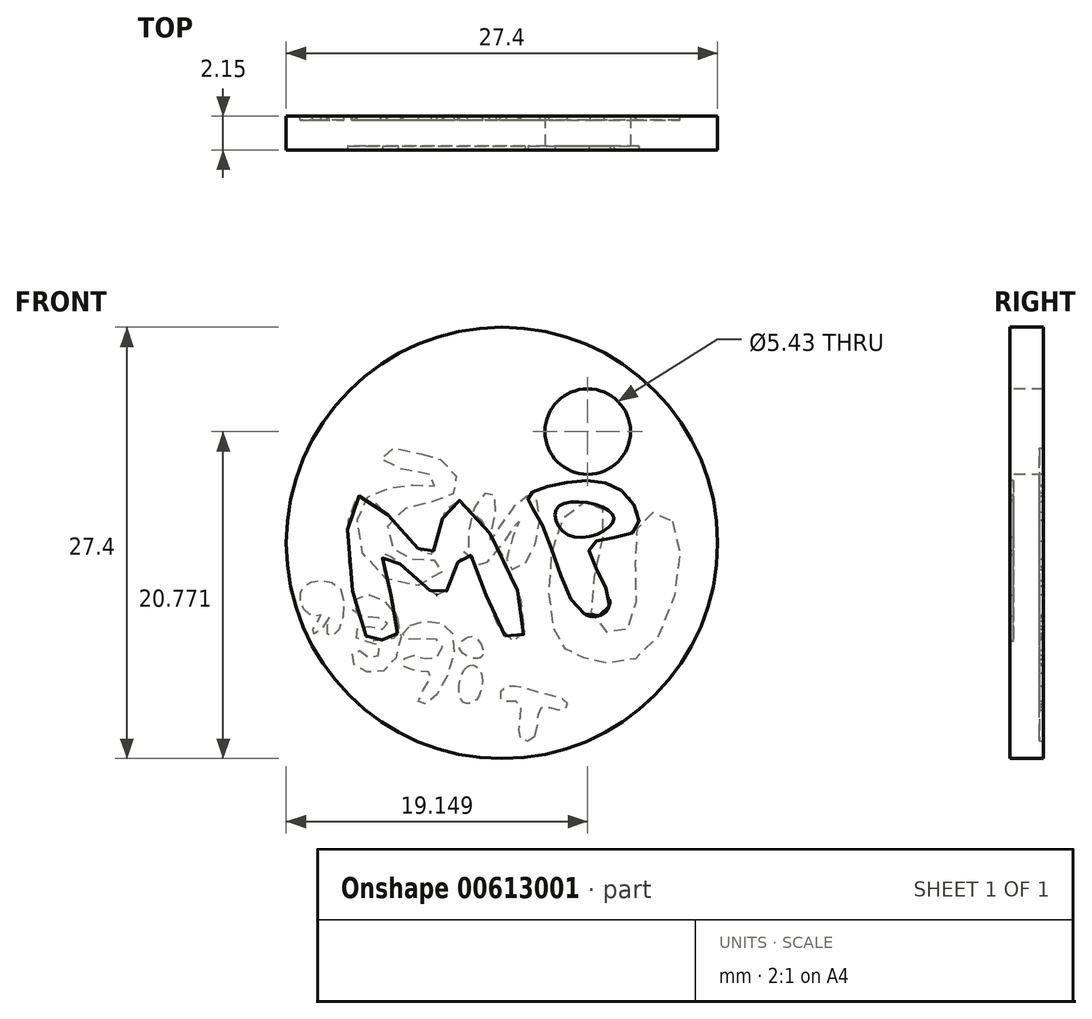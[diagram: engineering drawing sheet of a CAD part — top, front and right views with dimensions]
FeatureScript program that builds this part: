
annotation { "Feature Type Name" : "Feature", "Feature Type Description" : "" }
export const myFeature = defineFeature(function(context is Context, id is Id, definition is map)
    precondition{}
    {
        {
            var Q0;
            Q0=qCreatedBy(makeId("Front.planeOp"),FACE);
            var sketch = newSketch(context, id + "F0", { "sketchPlane" : qUnion([Q0])});
            skCircle(sketch, "E0", {"center": v(15.74, 15.61) * mm, "radius": 13.7 * mm});
            skPoint(sketch, "E1", {"position": v(16, 29.31) * mm});
            skPoint(sketch, "E2", {"position": v(16, 1.91) * mm});
            skSolve(sketch);
        }
        {
            var Q0;
            Q0 = qSketchRegion(id + "F0", true);
            extrude(context, id + "F1", {"entities" : qUnion([Q0]), "depth" : 2.15 * mm, "offsetDistance" : 25 * mm});
        }
        {
            var Q0;
            Q0=makeQuery(id+"F1.opExtrude","CAP_FACE",FACE,{"disambiguationData":[OSD([sQuery(id+"F0.wireOp",EDGE,"E0")])],"isStart":false});
            var sketch = newSketch(context, id + "F2", { "sketchPlane" : qUnion([Q0])});
            skCircle(sketch, "E3", {"center": v(21.19, 22.68) * mm, "radius": 2.71 * mm});
            skSolve(sketch);
        }
        {
            var Q0;
            Q0=makeQuery(id+"F2.imprint","IMPRINT",FACE,{"disambiguationData":[TD([[makeQuery(id+"F2.imprint","IMPRINT",EDGE,{"derivedFrom":sQuery(id+"F2.wireOp",EDGE,"E3")}),1.0]])]});
            extrude(context, id + "F3", {"entities" : qUnion([Q0]), "operationType" : NewBodyOperationType.REMOVE, "endBound" : BoundingType.UP_TO_NEXT, "oppositeDirection" : true, "depth" : 25 * mm, "offsetDistance" : 25 * mm});
        }
        {
            var Q0;
            Q0=makeQuery(id+"F1.opExtrude","CAP_FACE",FACE,{"disambiguationData":[OSD([sQuery(id+"F0.wireOp",EDGE,"E0")])],"isStart":false});
            var sketch = newSketch(context, id + "F4", { "sketchPlane" : qUnion([Q0])});
            skFitSpline(sketch, "E4", {"points": [v(7.1, 9.7) * mm, v(6.53, 18.53) * mm, v(10.66, 15.05) * mm, v(11.38, 15.08) * mm, v(12.81, 18.35) * mm, v(17.2, 10.16) * mm, v(16.05, 9.59) * mm, v(13.5, 15.08) * mm, v(12.27, 12.64) * mm, v(11.41, 12.42) * mm, v(8.21, 14.83) * mm, v(9.11, 9.87) * mm, v(8.1, 9.44) * mm, v(7.1, 9.7) * mm]});
            skFitSpline(sketch, "E5", {"points": [v(20.97, 11.1) * mm, v(18.24, 16.92) * mm, v(17.41, 18.57) * mm, v(19.93, 19.47) * mm, v(23.49, 18.82) * mm, v(24.2, 16.38) * mm, v(21.33, 15.44) * mm, v(22.59, 11.78) * mm, v(20.97, 11.1) * mm]});
            skFitSpline(sketch, "E6", {"points": [v(19.35, 17.96) * mm, v(20.18, 16.02) * mm, v(22.84, 17.27) * mm, v(19.35, 17.96) * mm]});
            skSolve(sketch);
        }
        {
            var Q0;
            Q0=makeQuery(id+"F4.imprint","IMPRINT",FACE,{"disambiguationData":[TD([[makeQuery(id+"F4.imprint","IMPRINT",EDGE,{"derivedFrom":sQuery(id+"F4.wireOp",EDGE,"E5")}),-1.0]])]});
            var Q1;
            Q1=makeQuery(id+"F4.imprint","IMPRINT",FACE,{"disambiguationData":[TD([[makeQuery(id+"F4.imprint","IMPRINT",EDGE,{"derivedFrom":sQuery(id+"F4.wireOp",EDGE,"E4")}),-1.0]])]});
            extrude(context, id + "F5", {"entities" : qUnion([Q0, Q1]), "operationType" : NewBodyOperationType.REMOVE, "oppositeDirection" : true, "depth" : 0.25 * mm, "hasOffset" : true, "offsetDistance" : 25 * mm});
        }
        {
            var Q0;
            Q0=makeQuery(id+"F1.opExtrude","CAP_FACE",FACE,{"disambiguationData":[OSD([sQuery(id+"F0.wireOp",EDGE,"E0")])],"isStart":true});
            var sketch = newSketch(context, id + "F6", { "sketchPlane" : qUnion([Q0])});
            skFitSpline(sketch, "E7", {"points": [v(-26.56, 16.99) * mm, v(-24.98, 8.8) * mm, v(-21.02, 8.28) * mm, v(-19.13, 9.9) * mm, v(-19.96, 17.62) * mm, v(-22.13, 17.71) * mm, v(-21.53, 10.75) * mm, v(-23.87, 10.32) * mm, v(-24.53, 16.96) * mm, v(-26.56, 16.99) * mm]});
            skFitSpline(sketch, "E8", {"points": [v(-17.24, 14.35) * mm, v(-17.96, 18.3) * mm, v(-16.84, 18.28) * mm, v(-14.95, 15.74) * mm, v(-15.34, 18.48) * mm, v(-14.43, 18.59) * mm, v(-13.7, 14.52) * mm, v(-14.75, 14.34) * mm, v(-16.85, 17.06) * mm, v(-16.06, 14.22) * mm, v(-17.24, 14.35) * mm]});
            skFitSpline(sketch, "E9", {"points": [v(-10.62, 21.27) * mm, v(-11.98, 20.82) * mm, v(-12.96, 19.43) * mm, v(-12.2, 18.44) * mm, v(-9.87, 17.9) * mm, v(-8.41, 16.38) * mm, v(-9.45, 14.72) * mm, v(-10.95, 14.59) * mm, v(-12.05, 14.09) * mm, v(-10.28, 12.89) * mm, v(-7.02, 14.71) * mm, v(-6.86, 18.12) * mm, v(-8.28, 19) * mm, v(-10.4, 19.3) * mm, v(-11.58, 19.3) * mm, v(-11.02, 20.03) * mm, v(-8.3, 20.61) * mm, v(-8.27, 21.5) * mm, v(-10.62, 21.27) * mm]});
            skFitSpline(sketch, "E10", {"points": [v(-17.82, 3.37) * mm, v(-18.24, 5.14) * mm, v(-19.61, 5.01) * mm, v(-19.9, 5.45) * mm, v(-18.09, 6.1) * mm, v(-15.87, 6.4) * mm, v(-15.7, 5.65) * mm, v(-16.85, 5.46) * mm, v(-16.85, 3.23) * mm, v(-17.82, 3.37) * mm]});
            skFitSpline(sketch, "E11", {"points": [v(-13.5, 7.74) * mm, v(-14.35, 7.5) * mm, v(-14.06, 5.6) * mm, v(-13.14, 5.64) * mm, v(-13.5, 7.74) * mm]});
            skFitSpline(sketch, "E12", {"points": [v(-14.53, 8.52) * mm, v(-13.93, 8.28) * mm, v(-13.05, 9.04) * mm, v(-13.93, 9.64) * mm, v(-14.53, 8.52) * mm]});
            skFitSpline(sketch, "E13", {"points": [v(-9.92, 10.36) * mm, v(-12.57, 9.95) * mm, v(-11.07, 5.47) * mm, v(-10.44, 5.63) * mm, v(-11.26, 7.3) * mm, v(-9.62, 7.65) * mm, v(-9.74, 8.45) * mm, v(-11.47, 8.27) * mm, v(-11.82, 9.37) * mm, v(-9.52, 9.55) * mm, v(-9.92, 10.36) * mm]});
            skFitSpline(sketch, "E14", {"points": [v(-9.09, 10.92) * mm, v(-8.24, 7.5) * mm, v(-6.23, 8.07) * mm, v(-6.53, 8.82) * mm, v(-7.6, 8.26) * mm, v(-7.97, 9.07) * mm, v(-6.59, 9.5) * mm, v(-6.72, 10.3) * mm, v(-8.33, 10.17) * mm, v(-8.31, 10.73) * mm, v(-6.38, 11.12) * mm, v(-6.74, 12.25) * mm, v(-9.09, 10.92) * mm]});
            skFitSpline(sketch, "E15", {"points": [v(-5.47, 12.68) * mm, v(-5.2, 9.85) * mm, v(-4.68, 9.8) * mm, v(-4.75, 10.87) * mm, v(-4.11, 9.94) * mm, v(-3.7, 9.96) * mm, v(-4.25, 11) * mm, v(-3.9, 10.98) * mm, v(-3.16, 11.42) * mm, v(-3, 12.58) * mm, v(-3.8, 13.16) * mm, v(-5.47, 12.68) * mm]});
            skFitSpline(sketch, "E16", {"points": [v(-4.9, 12.26) * mm, v(-4.98, 11.53) * mm, v(-3.66, 11.48) * mm, v(-3.6, 12.55) * mm, v(-4.88, 12.73) * mm, v(-4.9, 12.26) * mm]});
            skSolve(sketch);
        }
        {
            var Q0;
            Q0=makeQuery(id+"F6.imprint","IMPRINT",FACE,{"disambiguationData":[TD([[makeQuery(id+"F6.imprint","IMPRINT",EDGE,{"derivedFrom":sQuery(id+"F6.wireOp",EDGE,"E7")}),1.0]])]});
            var Q1;
            Q1=makeQuery(id+"F6.imprint","IMPRINT",FACE,{"disambiguationData":[TD([[makeQuery(id+"F6.imprint","IMPRINT",EDGE,{"derivedFrom":sQuery(id+"F6.wireOp",EDGE,"E8")}),-1.0]])]});
            var Q2;
            Q2=makeQuery(id+"F6.imprint","IMPRINT",FACE,{"disambiguationData":[TD([[makeQuery(id+"F6.imprint","IMPRINT",EDGE,{"derivedFrom":sQuery(id+"F6.wireOp",EDGE,"E9")}),1.0]])]});
            var Q3;
            Q3=makeQuery(id+"F6.imprint","IMPRINT",FACE,{"disambiguationData":[TD([[makeQuery(id+"F6.imprint","IMPRINT",EDGE,{"derivedFrom":sQuery(id+"F6.wireOp",EDGE,"E15")}),1.0]])]});
            var Q4;
            Q4=makeQuery(id+"F6.imprint","IMPRINT",FACE,{"disambiguationData":[TD([[makeQuery(id+"F6.imprint","IMPRINT",EDGE,{"derivedFrom":sQuery(id+"F6.wireOp",EDGE,"E14")}),1.0]])]});
            var Q5;
            Q5=makeQuery(id+"F6.imprint","IMPRINT",FACE,{"disambiguationData":[TD([[makeQuery(id+"F6.imprint","IMPRINT",EDGE,{"derivedFrom":sQuery(id+"F6.wireOp",EDGE,"E11")}),1.0]])]});
            var Q6;
            Q6=makeQuery(id+"F6.imprint","IMPRINT",FACE,{"disambiguationData":[TD([[makeQuery(id+"F6.imprint","IMPRINT",EDGE,{"derivedFrom":sQuery(id+"F6.wireOp",EDGE,"E10")}),-1.0]])]});
            var Q7;
            Q7=makeQuery(id+"F6.imprint","IMPRINT",FACE,{"disambiguationData":[TD([[makeQuery(id+"F6.imprint","IMPRINT",EDGE,{"derivedFrom":sQuery(id+"F6.wireOp",EDGE,"E12")}),1.0]])]});
            var Q8;
            Q8=makeQuery(id+"F6.imprint","IMPRINT",FACE,{"disambiguationData":[TD([[makeQuery(id+"F6.imprint","IMPRINT",EDGE,{"derivedFrom":sQuery(id+"F6.wireOp",EDGE,"E13")}),1.0]])]});
            var Q9;
            Q9=makeQuery(id+"F6.imprint","IMPRINT",FACE,{"disambiguationData":[TD([[makeQuery(id+"F6.imprint","IMPRINT",EDGE,{"derivedFrom":sQuery(id+"F6.wireOp",EDGE,"E16")}),1.0]])]});
            extrude(context, id + "F7", {"entities" : qUnion([Q0, Q1, Q2, Q3, Q4, Q5, Q6, Q7, Q8, Q9]), "operationType" : NewBodyOperationType.REMOVE, "oppositeDirection" : true, "depth" : 0.25 * mm, "offsetDistance" : 25 * mm});
        }
    });
